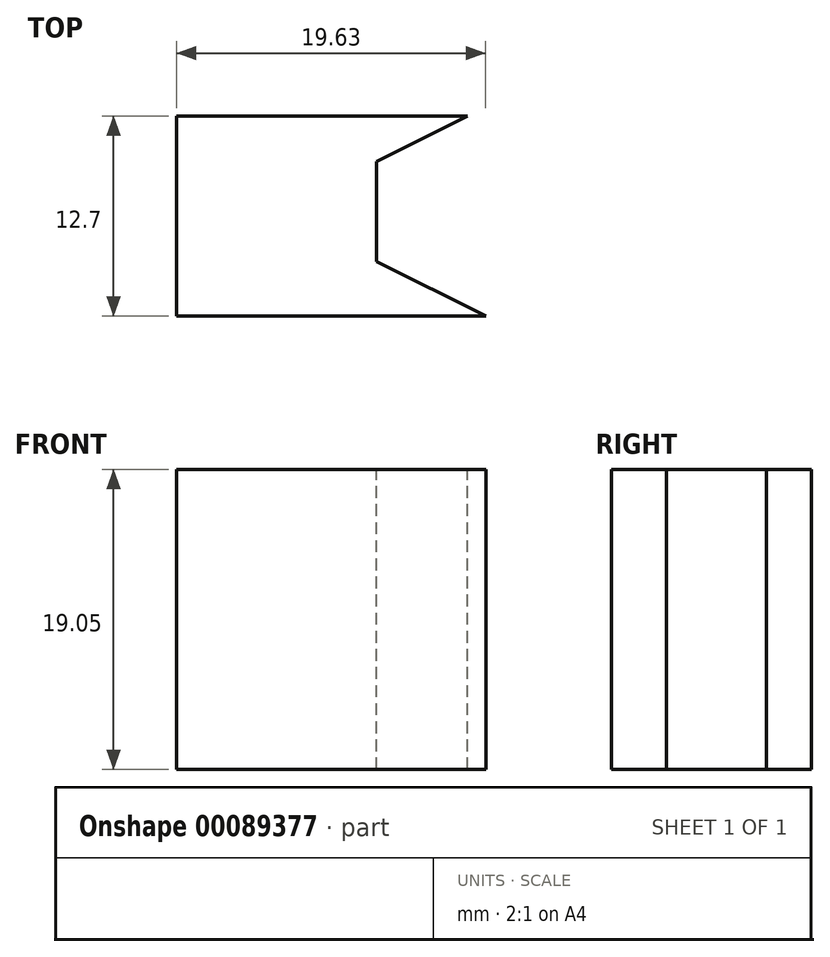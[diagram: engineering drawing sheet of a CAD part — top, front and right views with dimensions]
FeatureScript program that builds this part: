
annotation { "Feature Type Name" : "Feature", "Feature Type Description" : "" }
export const myFeature = defineFeature(function(context is Context, id is Id, definition is map)
    precondition{}
    {
        {
            var Q0;
            Q0=qCreatedBy(makeId("Front.planeOp"),FACE);
            cPlane(context, id + "F0", {"entities" : qUnion([Q0]), "cplaneType" : CPlaneType.OFFSET, "offset" : 50.8 * mm, "width" : 152.4 * mm, "height" : 152.4 * mm});
        }
        {
            var Q0;
            Q0=qCreatedBy(makeId("Right.planeOp"),FACE);
            cPlane(context, id + "F1", {"entities" : qUnion([Q0]), "cplaneType" : CPlaneType.OFFSET, "offset" : 50.8 * mm, "width" : 152.4 * mm, "height" : 152.4 * mm});
        }
        {
            var Q0;
            Q0=qCreatedBy(makeId("Top.planeOp"),FACE);
            cPlane(context, id + "F2", {"entities" : qUnion([Q0]), "cplaneType" : CPlaneType.OFFSET, "offset" : 50.8 * mm, "width" : 152.4 * mm, "height" : 152.4 * mm});
        }
        {
            var Q0;
            Q0=qCreatedBy(makeId("Front.planeOp"),FACE);
            var sketch = newSketch(context, id + "F3", { "sketchPlane" : qUnion([Q0])});
            skLineSegment(sketch, "E0.bottom", {"start": v(25.4, 25.4) * mm, "end": v(-25.4, 25.4) * mm});
            skLineSegment(sketch, "E0.top", {"start": v(25.4, -25.4) * mm, "end": v(-25.4, -25.4) * mm});
            skLineSegment(sketch, "E0.left", {"start": v(25.4, 25.4) * mm, "end": v(25.4, -25.4) * mm});
            skLineSegment(sketch, "E0.right", {"start": v(-25.4, 25.4) * mm, "end": v(-25.4, -25.4) * mm});
            skPoint(sketch, "E0.middle", {"position": v(0, 0) * mm});
            skSolve(sketch);
        }
        {
            var Q0;
            Q0=makeQuery(id+"F3.imprint","IMPRINT",FACE,{"disambiguationData":[TD([[makeQuery(id+"F3.imprint","IMPRINT",EDGE,{"derivedFrom":sQuery(id+"F3.wireOp",EDGE,"E0.bottom")}),1.0]])]});
            extrude(context, id + "F4", {"entities" : qUnion([Q0]), "depth" : 25.4 * mm});
        }
        {
            var Q0;
            Q0=makeQuery(id+"F4.opExtrude","CAP_FACE",FACE,{"disambiguationData":[OSD([sQuery(id+"F3.wireOp",EDGE,"E0.bottom"),sQuery(id+"F3.wireOp",EDGE,"E0.top"),sQuery(id+"F3.wireOp",EDGE,"E0.left"),sQuery(id+"F3.wireOp",EDGE,"E0.right")])],"isStart":true});
            extrude(context, id + "F5", {"entities" : qUnion([Q0]), "operationType" : NewBodyOperationType.ADD, "depth" : 25.4 * mm});
        }
        {
            var Q0;
            Q0=qCreatedBy(id+"F0.planeOp",FACE);
            var sketch = newSketch(context, id + "F6", { "sketchPlane" : qUnion([Q0])});
            skLineSegment(sketch, "E1", {"start": v(25.4, 25.4) * mm, "end": v(25.4, -25.4) * mm});
            skLineSegment(sketch, "E2", {"start": v(25.4, -25.4) * mm, "end": v(-25.4, -25.4) * mm});
            skLineSegment(sketch, "E3", {"start": v(-25.4, -25.4) * mm, "end": v(-25.4, 25.4) * mm});
            skLineSegment(sketch, "E4", {"start": v(-25.4, 25.4) * mm, "end": v(25.4, 25.4) * mm});
            skLineSegment(sketch, "E5", {"start": v(25.4, 19.05) * mm, "end": v(25.4, 6.35) * mm});
            skLineSegment(sketch, "E6", {"start": v(25.4, 6.35) * mm, "end": v(-12.7, 6.35) * mm});
            skLineSegment(sketch, "E7", {"start": v(-12.7, 6.35) * mm, "end": v(-12.7, 19.05) * mm});
            skLineSegment(sketch, "E8", {"start": v(-12.7, 19.05) * mm, "end": v(25.4, 19.05) * mm});
            skLineSegment(sketch, "E9", {"start": v(-25.4, -19.05) * mm, "end": v(12.7, -19.05) * mm});
            skLineSegment(sketch, "E10", {"start": v(12.7, -19.05) * mm, "end": v(12.7, -6.35) * mm});
            skLineSegment(sketch, "E11", {"start": v(12.7, -6.35) * mm, "end": v(-25.4, -6.35) * mm});
            skSolve(sketch);
        }
        {
            var Q0;
            Q0=makeQuery(id+"F6.imprint","IMPRINT",FACE,{"disambiguationData":[TD([[makeQuery(id+"F6.imprint","IMPRINT",EDGE,{"derivedFrom":sQuery(id+"F6.wireOp",EDGE,"E5")}),-1.0]])]});
            var Q1;
            {var subQ0=sQuery(id+"F6.wireOp",EDGE,"E9");Q1=makeQuery(id+"F6.imprint","IMPRINT",FACE,{"disambiguationData":[TD([[makeQuery(id+"F6.imprint","IMPRINT",EDGE,{"derivedFrom":subQ0}),1.0]])]});}
            extrude(context, id + "F7", {"entities" : qUnion([Q0, Q1]), "operationType" : NewBodyOperationType.REMOVE, "oppositeDirection" : true, "depth" : 76.2 * mm});
        }
        {
            var Q0;
            Q0=qCreatedBy(id+"F1.planeOp",FACE);
            var sketch = newSketch(context, id + "F8", { "sketchPlane" : qUnion([Q0])});
            skLineSegment(sketch, "E12", {"start": v(-25.4, 25.4) * mm, "end": v(-25.4, -25.4) * mm});
            skLineSegment(sketch, "E13", {"start": v(-25.4, -25.4) * mm, "end": v(25.4, -25.4) * mm});
            skLineSegment(sketch, "E14", {"start": v(25.4, -25.4) * mm, "end": v(25.4, 25.4) * mm});
            skLineSegment(sketch, "E15", {"start": v(25.4, 25.4) * mm, "end": v(-25.4, 25.4) * mm});
            skLineSegment(sketch, "E16", {"start": v(-6.35, -25.4) * mm, "end": v(-6.35, -6.35) * mm});
            skLineSegment(sketch, "E17", {"start": v(-6.35, -6.35) * mm, "end": v(6.35, -6.35) * mm});
            skLineSegment(sketch, "E18", {"start": v(6.35, -6.35) * mm, "end": v(6.35, -25.4) * mm});
            skLineSegment(sketch, "E19", {"start": v(6.35, -25.4) * mm, "end": v(25.4, -25.4) * mm});
            skLineSegment(sketch, "E20", {"start": v(25.4, 25.4) * mm, "end": v(6.35, 25.4) * mm});
            skLineSegment(sketch, "E21", {"start": v(6.35, 25.4) * mm, "end": v(6.35, 6.35) * mm});
            skLineSegment(sketch, "E22", {"start": v(6.35, 6.35) * mm, "end": v(-6.35, 6.35) * mm});
            skLineSegment(sketch, "E23", {"start": v(-6.35, 6.35) * mm, "end": v(-6.35, 25.4) * mm});
            skLineSegment(sketch, "E24", {"start": v(-6.35, 25.4) * mm, "end": v(-25.4, 25.4) * mm});
            skSolve(sketch);
        }
        {
            var Q0;
            Q0=makeQuery(id+"F8.imprint","IMPRINT",FACE,{"disambiguationData":[TD([[makeQuery(id+"F8.imprint","IMPRINT",EDGE,{"derivedFrom":sQuery(id+"F8.wireOp",EDGE,"E15")}),1.0]])]});
            var Q1;
            {var subQ2=sQuery(id+"F8.wireOp",EDGE,"E16");Q1=makeQuery(id+"F8.imprint","IMPRINT",FACE,{"disambiguationData":[TD([[makeQuery(id+"F8.imprint","IMPRINT",EDGE,{"derivedFrom":subQ2}),-1.0]])]});}
            extrude(context, id + "F9", {"entities" : qUnion([Q0, Q1]), "operationType" : NewBodyOperationType.REMOVE, "oppositeDirection" : true, "depth" : 76.2 * mm});
        }
        {
            var Q0;
            Q0=qCreatedBy(id+"F2.planeOp",FACE);
            var sketch = newSketch(context, id + "F10", { "sketchPlane" : qUnion([Q0])});
            skLineSegment(sketch, "E25", {"start": v(-25.4, 25.4) * mm, "end": v(25.4, 25.4) * mm});
            skLineSegment(sketch, "E26", {"start": v(25.4, 25.4) * mm, "end": v(25.4, -25.4) * mm});
            skLineSegment(sketch, "E27", {"start": v(25.4, -25.4) * mm, "end": v(-25.4, -25.4) * mm});
            skLineSegment(sketch, "E28", {"start": v(-25.4, -25.4) * mm, "end": v(-25.4, 25.4) * mm});
            skLineSegment(sketch, "E29", {"start": v(-25.4, 25.4) * mm, "end": v(25.4, 19.05) * mm});
            skLineSegment(sketch, "E30", {"start": v(25.4, 19.05) * mm, "end": v(25.4, 6.35) * mm});
            skLineSegment(sketch, "E31", {"start": v(25.4, 6.35) * mm, "end": v(12.7, 0) * mm});
            skLineSegment(sketch, "E32", {"start": v(12.7, 0) * mm, "end": v(25.4, -6.35) * mm});
            skLineSegment(sketch, "E33", {"start": v(25.4, -6.35) * mm, "end": v(25.4, -19.05) * mm});
            skLineSegment(sketch, "E34", {"start": v(25.4, -19.05) * mm, "end": v(-25.4, -25.4) * mm});
            skLineSegment(sketch, "E35", {"start": v(-25.4, -25.4) * mm, "end": v(-25.4, -12.63) * mm});
            skLineSegment(sketch, "E36", {"start": v(-25.4, -12.63) * mm, "end": v(0, -9.23) * mm});
            skLineSegment(sketch, "E37", {"start": v(0, -9.23) * mm, "end": v(-12.7, -2.88) * mm});
            skLineSegment(sketch, "E38", {"start": v(-12.7, -2.88) * mm, "end": v(-12.7, 3.47) * mm});
            skLineSegment(sketch, "E39", {"start": v(-12.7, 3.47) * mm, "end": v(0, 9.82) * mm});
            skLineSegment(sketch, "E40", {"start": v(0, 9.82) * mm, "end": v(-25.4, 13) * mm});
            skLineSegment(sketch, "E41", {"start": v(-25.4, 13) * mm, "end": v(-25.4, 25.4) * mm});
            skSolve(sketch);
        }
        {
            var Q0;
            {var subQ0=sQuery(id+"F10.wireOp",EDGE,"E31");Q0=makeQuery(id+"F10.imprint","IMPRINT",FACE,{"disambiguationData":[TD([[makeQuery(id+"F10.imprint","IMPRINT",EDGE,{"derivedFrom":subQ0}),1.0]])]});}
            var Q1;
            Q1=makeQuery(id+"F10.imprint","IMPRINT",FACE,{"disambiguationData":[TD([[makeQuery(id+"F10.imprint","IMPRINT",EDGE,{"derivedFrom":sQuery(id+"F10.wireOp",EDGE,"E28")}),-1.0]])]});
            extrude(context, id + "F11", {"entities" : qUnion([Q0, Q1]), "operationType" : NewBodyOperationType.REMOVE, "oppositeDirection" : true, "depth" : 76.2 * mm});
        }
    });
